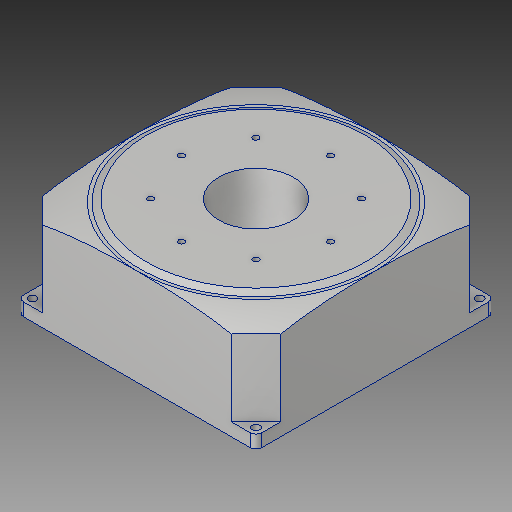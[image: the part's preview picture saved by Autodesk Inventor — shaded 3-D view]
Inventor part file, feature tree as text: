
AUTODESK INVENTOR PART (.ipt)
format: ipt  version: 2019 (Build 230136000, 136)  size: 256,000 bytes
history: native  units: mm
features: sketch x11, extrude x6, fillet x4, hole x2, revolve x2, plane x1
ambient origin geometry x8: Origin, YZ Plane, XZ Plane, XY Plane, X Axis, Y Axis, Z Axis, Center Point
bodies: Solid1 (feature_tree)
feature tree (26):
  sketch  "Sketch1"  dims[d0=240.0mm d1=240.0mm d3=120.0mm d4=120.0mm d5=75.0mm d6=100.0mm d7=0.0mm]
  extrude  "Extrusion1"  Depth=240.0mm
  fillet  "Fillet1"  Radius=120.0mm
  fillet  "Fillet2"  Radius=120.0mm
  fillet  "Fillet3"  Radius=75.0mm
  fillet  "Fillet4"  Radius=100.0mm
  hole  "Hole1"  [1 undecoded]
  hole  "Hole2"  [1 undecoded]
  extrude  "Extrusion2"  Depth=53.033009mm
  extrude  "Extrusion3"  Depth=53.033009mm
  extrude  "Extrusion4"  Depth=53.033009mm
  extrude  "Extrusion5"  Depth=10.0mm
  extrude  "Extrusion6"  TaperAngle=45.0deg  [1 undecoded]
  plane  "Work Plane1"
  revolve  "Revolution1"  [1 undecoded]
  revolve  "Revolution2"  [1 undecoded]
  sketch  "Sketch2"  dims[d8=6.0mm d9=6.0mm]
  sketch  "Sketch3"  dims[d10=6.0mm d11=6.0mm]
  sketch  "Sketch4"  dims[d14=53.033009mm d15=53.033009mm]
  sketch  "Sketch5"  dims[d16=53.033009mm d17=53.033009mm]
  sketch  "Sketch6"  dims[d18=53.033009mm d19=53.033009mm]
  sketch  "Sketch7"  dims[d20=6.0mm d21=6.0mm d22=4.0mm d23=2.0mm d24=90.0deg d25=10.0mm d26=20.594885mm]
  sketch  "Sketch8"  dims[d27=8.0mm d28=6.0mm d29=4.0mm d30=2.0mm d31=90.0deg d32=10.0mm d33=20.594885mm d34=112.5mm]
  sketch  "Sketch9"  dims[d35=112.5mm d36=45.0deg]
  sketch  "Sketch10"  dims[d38=135.0deg d39=87.0mm d40=0.0mm]
  sketch  "Sketch11"  dims[d41=135.0deg d42=87.0mm d43=0.0mm d44=135.0deg d45=87.0mm d46=0.0mm d47=45.0deg d48=87.0mm d49=0.0mm d50=233.5mm d51=3.0mm d52=0.0mm d53=240.0mm d54=240.0mm d55=90.0deg d61=90.0deg d62=105.0deg d63=200.0mm d64=120.0mm d65=3.0mm d66=11.34464mm d67=90.0deg]
note: 5 required parameter values undecoded (feature->parameter linkage not recoverable at this tier; creation-order binding heuristic only, values carry confidence <= 0.55)